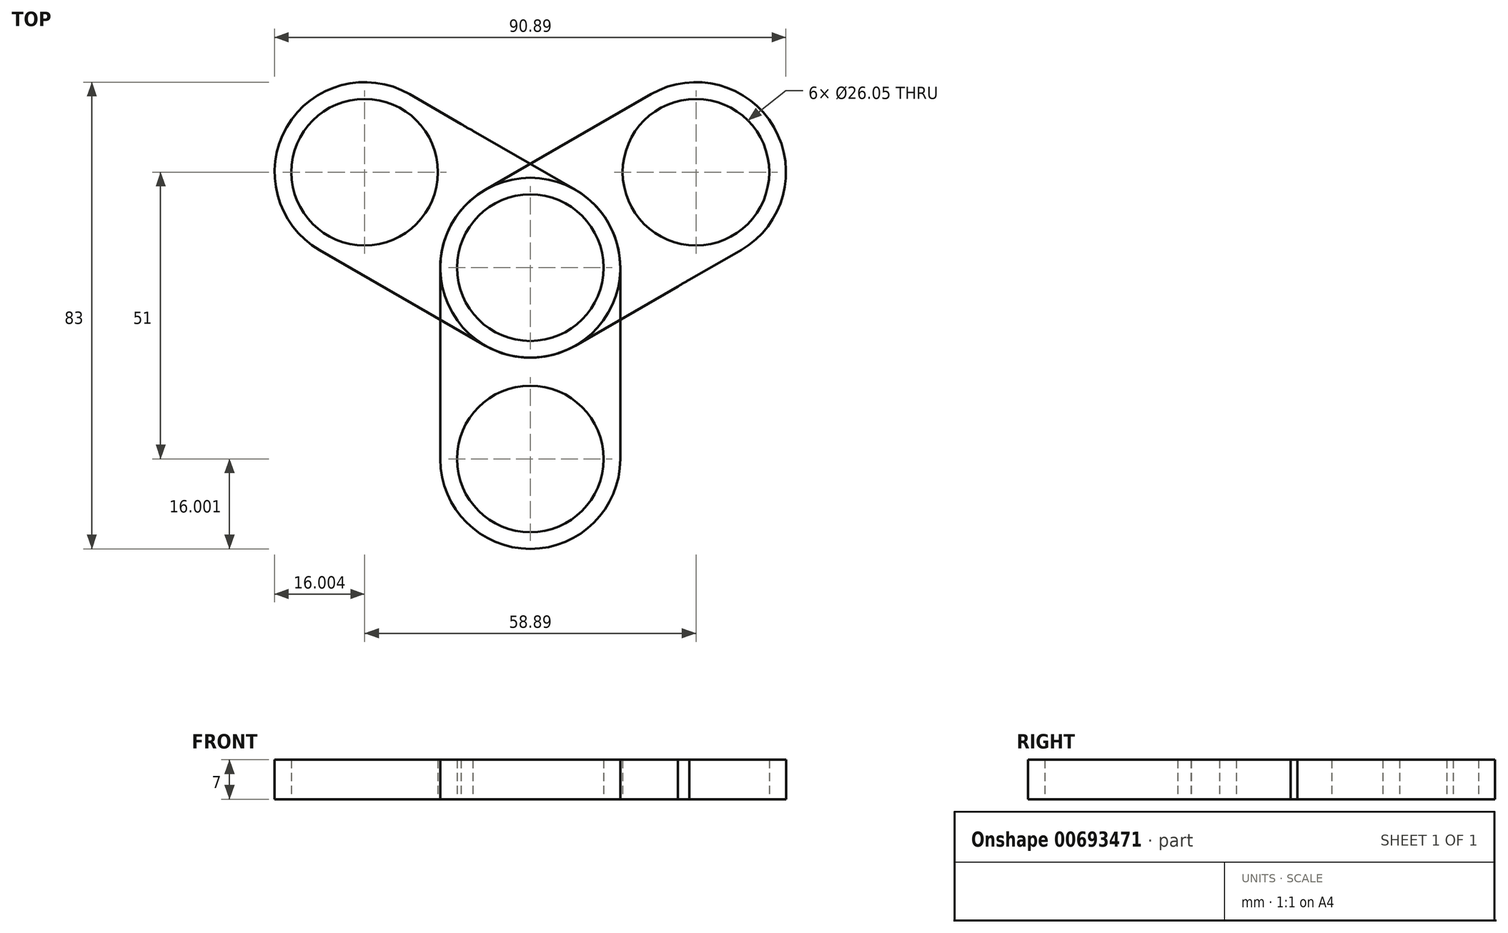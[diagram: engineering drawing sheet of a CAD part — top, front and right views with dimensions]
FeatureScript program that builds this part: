
annotation { "Feature Type Name" : "Feature", "Feature Type Description" : "" }
export const myFeature = defineFeature(function(context is Context, id is Id, definition is map)
    precondition{}
    {
        {
            var Q0;
            Q0=qCreatedBy(makeId("Top.planeOp"),FACE);
            var sketch = newSketch(context, id + "F0", { "sketchPlane" : qUnion([Q0])});
            skLineSegment(sketch, "E0.bottom", {"start": v(-31.86, 21.04) * mm, "end": v(0.14, 21.04) * mm});
            skLineSegment(sketch, "E0.top", {"start": v(-31.86, -12.96) * mm, "end": v(0.14, -12.96) * mm});
            skLineSegment(sketch, "E0.left", {"start": v(-31.86, 21.04) * mm, "end": v(-31.86, -12.96) * mm});
            skLineSegment(sketch, "E0.right", {"start": v(0.14, 21.04) * mm, "end": v(0.14, -12.96) * mm});
            skCircle(sketch, "E1", {"center": v(-15.86, -12.96) * mm, "radius": 13.03 * mm});
            skCircle(sketch, "E2", {"center": v(-15.86, 21.04) * mm, "radius": 13.03 * mm});
            skCircle(sketch, "E3", {"center": v(-15.86, 21.04) * mm, "radius": 16 * mm});
            skCircle(sketch, "E4", {"center": v(-15.86, -12.96) * mm, "radius": 16 * mm});
            skLineSegment(sketch, "E5", {"start": v(-30.18, -20.1) * mm, "end": v(-1.54, -20.1) * mm});
            skArc(sketch, "E6", {"start": v(-56.08, -24.42) * mm, "mid": v(-38.57, -17.56) * mm, "end": v(-31.86, 0) * mm});
            skArc(sketch, "E7", {"start": v(-56.08, -24.42) * mm, "mid": v(-31.21, -34.38) * mm, "end": v(-5.94, -25.5) * mm});
            skCircle(sketch, "E8", {"center": v(-15.86, 21.04) * mm, "radius": 50 * mm});
            skSolve(sketch);
        }
        {
            var Q0;
            {var subQ0=sQuery(id+"F0.wireOp",EDGE,"E0.left");Q0=makeQuery(id+"F0.imprint","IMPRINT",FACE,{"disambiguationData":[TD([[makeQuery(id+"F0.imprint","IMPRINT",EDGE,{"derivedFrom":subQ0}),1.0]])]});}
            var Q1;
            {var subQ1=sQuery(id+"F0.wireOp",EDGE,"E0.bottom");var subQ3=sQuery(id+"F0.wireOp",EDGE,"E2");var subQ4=makeQuery(id+"F0.imprint","INTERSECT",VERTEX,{"disambiguationData":[OD(0.0)],"derivedFrom":[subQ1,subQ3]});Q1=makeQuery(id+"F0.imprint","IMPRINT",FACE,{"disambiguationData":[TD([[makeQuery(id+"F0.imprint","IMPRINT",EDGE,{"disambiguationData":[TD([[subQ4,-1.0]])],"derivedFrom":subQ3}),-1.0]])]});}
            var Q2;
            {var subQ1=sQuery(id+"F0.wireOp",EDGE,"E0.bottom");var subQ3=sQuery(id+"F0.wireOp",EDGE,"E2");var subQ4=makeQuery(id+"F0.imprint","INTERSECT",VERTEX,{"disambiguationData":[OD(0.0)],"derivedFrom":[subQ1,subQ3]});Q2=makeQuery(id+"F0.imprint","IMPRINT",FACE,{"disambiguationData":[TD([[makeQuery(id+"F0.imprint","IMPRINT",EDGE,{"disambiguationData":[TD([[subQ4,1.0]])],"derivedFrom":subQ3}),-1.0]])]});}
            var Q3;
            {var subQ1=sQuery(id+"F0.wireOp",EDGE,"E0.top");var subQ3=sQuery(id+"F0.wireOp",EDGE,"E1");var subQ4=makeQuery(id+"F0.imprint","INTERSECT",VERTEX,{"disambiguationData":[OD(0.0)],"derivedFrom":[subQ1,subQ3]});Q3=makeQuery(id+"F0.imprint","IMPRINT",FACE,{"disambiguationData":[TD([[makeQuery(id+"F0.imprint","IMPRINT",EDGE,{"disambiguationData":[TD([[subQ4,1.0]])],"derivedFrom":subQ3}),-1.0]])]});}
            var Q4;
            {var subQ1=sQuery(id+"F0.wireOp",EDGE,"E0.top");var subQ3=sQuery(id+"F0.wireOp",EDGE,"E1");var subQ4=makeQuery(id+"F0.imprint","INTERSECT",VERTEX,{"disambiguationData":[OD(0.0)],"derivedFrom":[subQ1,subQ3]});Q4=makeQuery(id+"F0.imprint","IMPRINT",FACE,{"disambiguationData":[TD([[makeQuery(id+"F0.imprint","IMPRINT",EDGE,{"disambiguationData":[TD([[subQ4,-1.0]])],"derivedFrom":subQ3}),-1.0]])]});}
            var Q5;
            {var subQ1=sQuery(id+"F0.wireOp",EDGE,"E0.top");var subQ3=sQuery(id+"F0.wireOp",EDGE,"E1");var subQ4=makeQuery(id+"F0.imprint","INTERSECT",VERTEX,{"disambiguationData":[OD(1.0)],"derivedFrom":[subQ1,subQ3]});Q5=makeQuery(id+"F0.imprint","IMPRINT",FACE,{"disambiguationData":[TD([[makeQuery(id+"F0.imprint","IMPRINT",EDGE,{"disambiguationData":[TD([[subQ4,-1.0]])],"derivedFrom":subQ3}),-1.0]])]});}
            var Q6;
            {var subQ0=sQuery(id+"F0.wireOp",EDGE,"E0.right");Q6=makeQuery(id+"F0.imprint","IMPRINT",FACE,{"disambiguationData":[TD([[makeQuery(id+"F0.imprint","IMPRINT",EDGE,{"derivedFrom":subQ0}),-1.0]])]});}
            var Q7;
            {var subQ1=sQuery(id+"F0.wireOp",EDGE,"E0.bottom");var subQ3=sQuery(id+"F0.wireOp",EDGE,"E2");var subQ4=makeQuery(id+"F0.imprint","INTERSECT",VERTEX,{"disambiguationData":[OD(1.0)],"derivedFrom":[subQ1,subQ3]});Q7=makeQuery(id+"F0.imprint","IMPRINT",FACE,{"disambiguationData":[TD([[makeQuery(id+"F0.imprint","IMPRINT",EDGE,{"disambiguationData":[TD([[subQ4,1.0]])],"derivedFrom":subQ3}),-1.0]])]});}
            var Q8;
            {var subQ1=sQuery(id+"F0.wireOp",EDGE,"E0.top");var subQ3=sQuery(id+"F0.wireOp",EDGE,"E1");var subQ4=makeQuery(id+"F0.imprint","INTERSECT",VERTEX,{"disambiguationData":[OD(1.0)],"derivedFrom":[subQ1,subQ3]});Q8=makeQuery(id+"F0.imprint","IMPRINT",FACE,{"disambiguationData":[TD([[makeQuery(id+"F0.imprint","IMPRINT",EDGE,{"disambiguationData":[TD([[subQ4,1.0]])],"derivedFrom":subQ3}),-1.0]])]});}
            var Q9;
            {var subQ0=sQuery(id+"F0.wireOp",EDGE,"E5");var subQ1=sQuery(id+"F0.wireOp",EDGE,"E1");var subQ2=makeQuery(id+"F0.imprint","INTERSECT",VERTEX,{"disambiguationData":[OD(0.0)],"derivedFrom":[subQ1,subQ0]});Q9=makeQuery(id+"F0.imprint","IMPRINT",FACE,{"disambiguationData":[TD([[makeQuery(id+"F0.imprint","IMPRINT",EDGE,{"disambiguationData":[TD([[subQ2,-1.0]])],"derivedFrom":subQ1}),-1.0]])]});}
            extrude(context, id + "F1", {"entities" : qUnion([Q0, Q1, Q2, Q3, Q4, Q5, Q6, Q7, Q8, Q9]), "depth" : 7 * mm, "offsetDistance" : 25 * mm});
        }
        {
            var Q0;
            Q0=makeQuery(id+"F1.opExtrude","SWEPT_BODY",BODY,{"disambiguationData":[OSD([sQuery(id+"F0.wireOp",EDGE,"E0.left"),sQuery(id+"F0.wireOp",EDGE,"E0.right"),sQuery(id+"F0.wireOp",EDGE,"E1"),sQuery(id+"F0.wireOp",EDGE,"E2"),sQuery(id+"F0.wireOp",EDGE,"E3"),sQuery(id+"F0.wireOp",EDGE,"E4")])]});
            var Q1;
            Q1=makeQuery(id+"F1.opExtrude","SWEPT_FACE",FACE,{"disambiguationData":[OSD([sQuery(id+"F0.wireOp",EDGE,"E3")])]});
            circularPattern(context, id + "F2", {"entities" : qUnion([Q0]), "axis" : qUnion([Q1]), "angle" : 360 * degree, "instanceCount" : 3, "equalSpace" : true});
        }
    });
